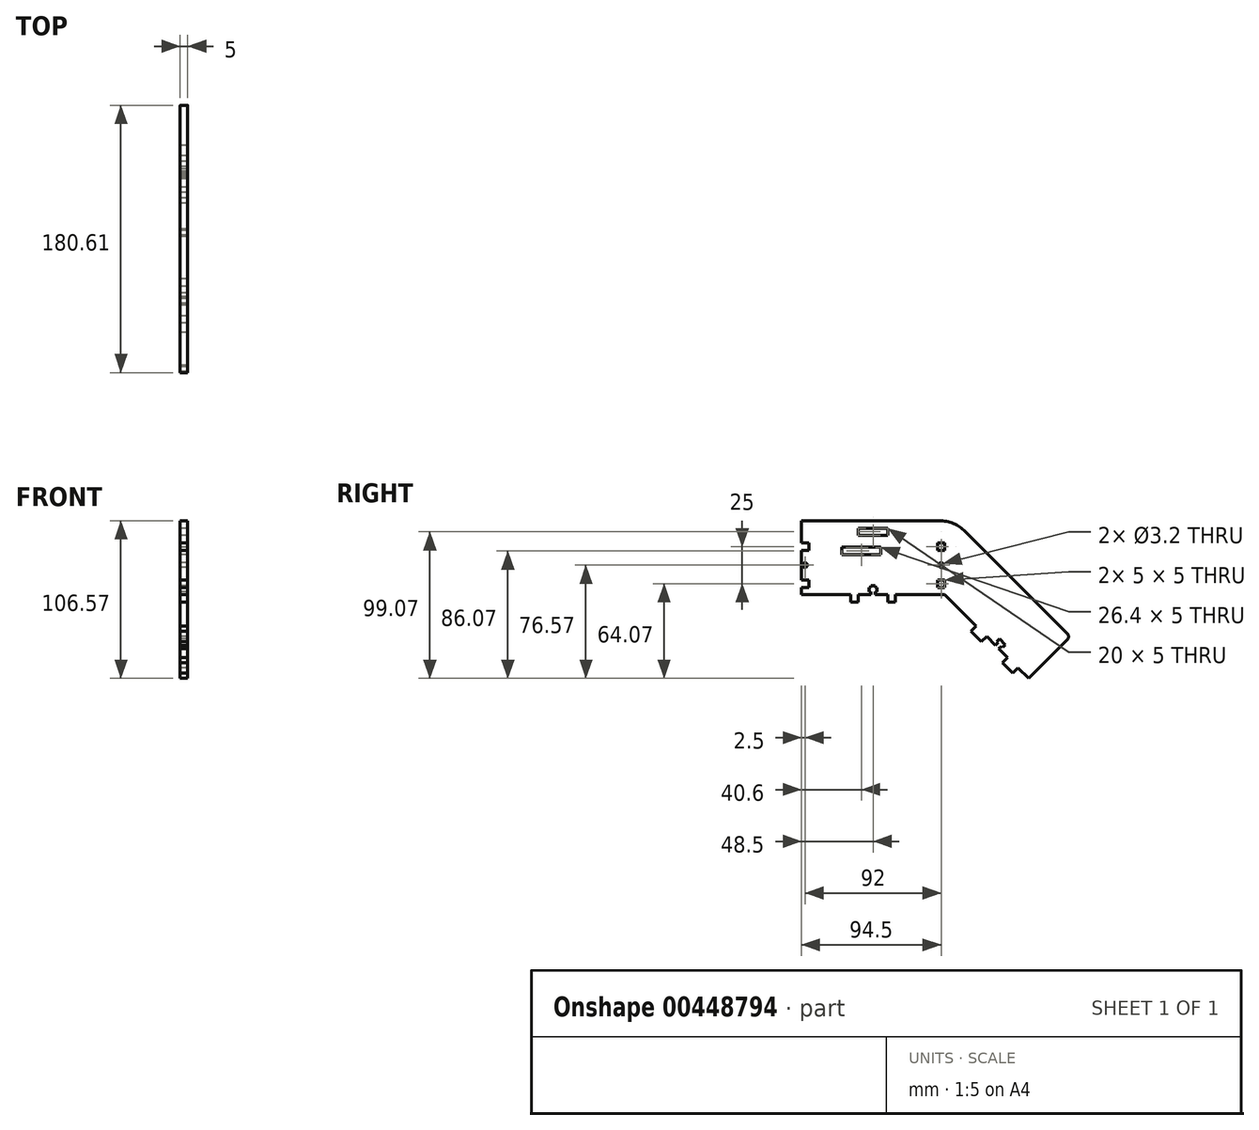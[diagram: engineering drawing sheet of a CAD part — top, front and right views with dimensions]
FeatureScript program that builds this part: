
annotation { "Feature Type Name" : "Feature", "Feature Type Description" : "" }
export const myFeature = defineFeature(function(context is Context, id is Id, definition is map)
    precondition{}
    {
        {
            assignVariable(context, id + "F0", {"name" : "thickness", "anyValue" : 5 * mm});
        }
        {
            var Q0;
            Q0=qCreatedBy(makeId("Right.planeOp"),FACE);
            var sketch = newSketch(context, id + "F1", { "sketchPlane" : qUnion([Q0])});
            skLineSegment(sketch, "E0.bottom", {"start": v(0, 0) * mm, "end": v(33.5, 0) * mm});
            skLineSegment(sketch, "E0.left", {"start": v(0, 0) * mm, "end": v(0, 5) * mm});
            skLineSegment(sketch, "E1", {"start": v(38.5, 45) * mm, "end": v(38.5, 40) * mm});
            skLineSegment(sketch, "E2", {"start": v(58.5, 40) * mm, "end": v(58.5, 45) * mm});
            skCircle(sketch, "E3", {"center": v(2.5, 20) * mm, "radius": 1.6 * mm});
            skLineSegment(sketch, "E4", {"start": v(0, 35) * mm, "end": v(5, 35) * mm});
            skLineSegment(sketch, "E5", {"start": v(5, 35) * mm, "end": v(5, 30) * mm});
            skLineSegment(sketch, "E6", {"start": v(5, 30) * mm, "end": v(0, 30) * mm});
            skLineSegment(sketch, "E7", {"start": v(0, 10) * mm, "end": v(5, 10) * mm});
            skLineSegment(sketch, "E8", {"start": v(5, 10) * mm, "end": v(5, 5) * mm});
            skLineSegment(sketch, "E9", {"start": v(5, 5) * mm, "end": v(0, 5) * mm});
            skLineSegment(sketch, "E10.trimOffspring", {"start": v(0, 10) * mm, "end": v(0, 30) * mm});
            skLineSegment(sketch, "E11.trimOffspring", {"start": v(50, 0) * mm, "end": v(58.5, 0) * mm});
            skLineSegment(sketch, "E12.bottom", {"start": v(27.4, 32) * mm, "end": v(53.8, 32) * mm});
            skLineSegment(sketch, "E12.top", {"start": v(27.4, 27) * mm, "end": v(53.8, 27) * mm});
            skLineSegment(sketch, "E12.left", {"start": v(27.4, 32) * mm, "end": v(27.4, 27) * mm});
            skLineSegment(sketch, "E12.right", {"start": v(53.8, 32) * mm, "end": v(53.8, 27) * mm});
            skLineSegment(sketch, "E13.MirrorCS", {"start": v(47, 2) * mm, "end": v(45.75, 2) * mm});
            skLineSegment(sketch, "E14.MirrorCS", {"start": v(51.25, 5) * mm, "end": v(51.25, 2) * mm});
            skLineSegment(sketch, "E15.MirrorCS", {"start": v(47, 6) * mm, "end": v(50, 6) * mm});
            skLineSegment(sketch, "E16.MirrorCS", {"start": v(51.25, 2) * mm, "end": v(50, 2) * mm});
            skLineSegment(sketch, "E17.MirrorCS", {"start": v(47, 0) * mm, "end": v(47, 2) * mm});
            skLineSegment(sketch, "E18.MirrorCS", {"start": v(50, 5) * mm, "end": v(51.25, 5) * mm});
            skLineSegment(sketch, "E19.MirrorCS", {"start": v(45.75, 5) * mm, "end": v(47, 5) * mm});
            skLineSegment(sketch, "E20.MirrorCS", {"start": v(45.75, 2) * mm, "end": v(45.75, 5) * mm});
            skLineSegment(sketch, "E21.MirrorCS", {"start": v(50, 2) * mm, "end": v(50, 0) * mm});
            skLineSegment(sketch, "E22.MirrorCS", {"start": v(47, 5) * mm, "end": v(47, 6) * mm});
            skLineSegment(sketch, "E23.MirrorCS", {"start": v(50, 6) * mm, "end": v(50, 5) * mm});
            skLineSegment(sketch, "E24.MirrorCS", {"start": v(58.5, 0) * mm, "end": v(58.5, -5) * mm});
            skLineSegment(sketch, "E25.MirrorCS", {"start": v(38.5, -5) * mm, "end": v(38.5, 0) * mm});
            skLineSegment(sketch, "E26.MirrorCS", {"start": v(63.5, -5) * mm, "end": v(63.5, 0) * mm});
            skLineSegment(sketch, "E27.MirrorCS", {"start": v(33.5, 0) * mm, "end": v(33.5, -5) * mm});
            skLineSegment(sketch, "E28.MirrorCS", {"start": v(38.5, 0) * mm, "end": v(47, 0) * mm});
            skPoint(sketch, "E29.MirrorP", {"position": v(48.5, 6) * mm});
            skLineSegment(sketch, "E30.MirrorCS", {"start": v(58.5, -5) * mm, "end": v(63.5, -5) * mm});
            skLineSegment(sketch, "E31.MirrorCS", {"start": v(33.5, -5) * mm, "end": v(38.5, -5) * mm});
            skLineSegment(sketch, "E32.trimOffspring", {"start": v(63.5, 0) * mm, "end": v(97, 0) * mm});
            skLineSegment(sketch, "E33", {"start": v(97, 0) * mm, "end": v(131.22, -34.22) * mm});
            skLineSegment(sketch, "E34", {"start": v(153.57, -56.57) * mm, "end": v(179.73, -30.4) * mm});
            skLineSegment(sketch, "E35", {"start": v(179.73, -26.16) * mm, "end": v(110.9, 42.68) * mm});
            skLineSegment(sketch, "E36", {"start": v(97, 0) * mm, "end": v(110.03, 43.54) * mm, "construction": true});
            skLineSegment(sketch, "E37", {"start": v(146.5, -49.5) * mm, "end": v(142.96, -53.03) * mm});
            skLineSegment(sketch, "E38", {"start": v(142.96, -53.03) * mm, "end": v(135.9, -45.96) * mm});
            skLineSegment(sketch, "E39", {"start": v(135.9, -45.96) * mm, "end": v(139.43, -42.43) * mm});
            skLineSegment(sketch, "E40", {"start": v(125.28, -28.28) * mm, "end": v(121.75, -31.82) * mm});
            skLineSegment(sketch, "E41", {"start": v(121.75, -31.82) * mm, "end": v(114.68, -24.75) * mm});
            skLineSegment(sketch, "E42", {"start": v(114.68, -24.75) * mm, "end": v(118.21, -21.21) * mm});
            skLineSegment(sketch, "E43", {"start": v(125.28, -28.28) * mm, "end": v(131.22, -34.22) * mm, "construction": true});
            skLineSegment(sketch, "E44", {"start": v(132.36, -35.36) * mm, "end": v(160.64, -7.07) * mm, "construction": true});
            skLineSegment(sketch, "E45", {"start": v(131.22, -34.22) * mm, "end": v(133, -32.46) * mm});
            skLineSegment(sketch, "E46", {"start": v(133, -32.46) * mm, "end": v(132.18, -31.64) * mm});
            skLineSegment(sketch, "E47", {"start": v(132.18, -31.64) * mm, "end": v(133.95, -29.88) * mm});
            skLineSegment(sketch, "E48", {"start": v(133.95, -29.88) * mm, "end": v(135.9, -31.82) * mm});
            skLineSegment(sketch, "E49.MirrorCS", {"start": v(137.84, -33.76) * mm, "end": v(135.9, -31.82) * mm});
            skLineSegment(sketch, "E50.MirrorCS", {"start": v(136.07, -35.53) * mm, "end": v(137.84, -33.76) * mm});
            skLineSegment(sketch, "E51.MirrorCS", {"start": v(135.25, -34.72) * mm, "end": v(136.07, -35.53) * mm});
            skLineSegment(sketch, "E52.MirrorCS", {"start": v(133.49, -36.49) * mm, "end": v(135.25, -34.72) * mm});
            skLineSegment(sketch, "E53.trimOffspring", {"start": v(133.49, -36.49) * mm, "end": v(139.43, -42.43) * mm, "construction": true});
            skLineSegment(sketch, "E54.trimOffspring", {"start": v(133.49, -36.49) * mm, "end": v(153.57, -56.57) * mm});
            skPoint(sketch, "E55.visualSharp", {"position": v(110.03, 43.54) * mm});
            skPoint(sketch, "E56.visualSharp", {"position": v(181.85, -28.28) * mm});
            skArc(sketch, "E56.filletArc", {"start": v(179.73, -30.4) * mm, "mid": v(180.61, -28.28) * mm, "end": v(179.73, -26.16) * mm});
            skPoint(sketch, "E57", {"position": v(2.5, 30) * mm});
            skLineSegment(sketch, "E58", {"start": v(0, 50) * mm, "end": v(93.21, 50) * mm});
            skLineSegment(sketch, "E59", {"start": v(38.5, 45) * mm, "end": v(58.5, 45) * mm});
            skLineSegment(sketch, "E60", {"start": v(38.5, 40) * mm, "end": v(58.5, 40) * mm});
            skLineSegment(sketch, "E61", {"start": v(0, 35) * mm, "end": v(0, 50) * mm});
            skPoint(sketch, "E62.visualSharp", {"position": v(103.57, 50) * mm});
            skArc(sketch, "E62.filletArc", {"start": v(110.9, 42.68) * mm, "mid": v(102.78, 48.1) * mm, "end": v(93.21, 50) * mm});
            skLineSegment(sketch, "E63", {"start": v(97, 0) * mm, "end": v(97, 49.71) * mm, "construction": true});
            skLineSegment(sketch, "E64.bottom", {"start": v(97, 5) * mm, "end": v(92, 5) * mm});
            skLineSegment(sketch, "E64.top", {"start": v(97, 10) * mm, "end": v(92, 10) * mm});
            skLineSegment(sketch, "E64.left", {"start": v(97, 5) * mm, "end": v(97, 10) * mm});
            skLineSegment(sketch, "E64.right", {"start": v(92, 5) * mm, "end": v(92, 10) * mm});
            skLineSegment(sketch, "E65.MirrorCS", {"start": v(97, 35) * mm, "end": v(92, 35) * mm});
            skLineSegment(sketch, "E66.MirrorCS", {"start": v(97, 30) * mm, "end": v(92, 30) * mm});
            skLineSegment(sketch, "E67.MirrorCS", {"start": v(97, 35) * mm, "end": v(97, 30) * mm});
            skLineSegment(sketch, "E68.MirrorCS", {"start": v(92, 35) * mm, "end": v(92, 30) * mm});
            skCircle(sketch, "E69", {"center": v(94.5, 20) * mm, "radius": 1.6 * mm});
            skPoint(sketch, "E69.centerSnap0", {"position": v(94.5, 30) * mm});
            skSolve(sketch);
        }
        {
            var Q0;
            Q0=qSketchRegion(id+"F1",true);
            extrude(context, id + "F2", {"entities" : qUnion([Q0]), "depth" : getVariable(context, 'thickness')});
        }
    });
